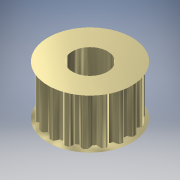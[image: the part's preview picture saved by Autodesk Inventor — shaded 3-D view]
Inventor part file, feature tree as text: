
AUTODESK INVENTOR PART (.ipt)
format: ipt  version: 2016 (Build 200138000, 138)  size: 373,760 bytes
history: native  units: mm (DEFAULTED — no unit token found)
features: plane x4, sketch x4, other x3, extrude x2, projected_geometry x2, revolve x1, mirror x1
ambient origin geometry x8: Origin, YZ Plane, XZ Plane, XY Plane, X Axis, Y Axis, Z Axis, Center Point
bodies: Solid1 (feature_tree)
feature tree (17):
  extrude  "Extrusion1"  Depth=7.0mm TaperAngle=0.0deg
  plane  "Work Plane2"
  plane  "Work Plane8"
  plane  "Work Plane9"
  other  "Spur Gear"
  extrude  "Extrusion2"  Depth=10.0mm TaperAngle=0.0deg
  revolve  "Revolution1"  [1 undecoded]
  plane  "Work Plane11"
  mirror  "Mirror1"
  sketch  "Sketch1"  dims[d0=11.0mm d1=7.0mm d2=0.0mm]
  sketch  "Sketch2"  dims[d3=45.714286mm d4=10.0mm d5=0.0mm]
  other  "Srf1"
  sketch  "Sketch3"  dims[d16=80.0mm d17=0.0mm d34=1.745329mm]
  sketch  "Sketch4"  dims[d39=0.0mm d41=0.0mm d43=80.0mm d46=80.0mm d47=0.0mm d48=0.0mm d49=5.0mm d50=10.0mm d51=0.0mm d52=0.5mm d53=90.0deg]
  other  "Pitch Diameter"
  projected_geometry  "Project Cut Edges1"
  projected_geometry  "Project Cut Edges2"
note: 1 required parameter value undecoded (feature->parameter linkage not recoverable at this tier; creation-order binding heuristic only, values carry confidence <= 0.55)
